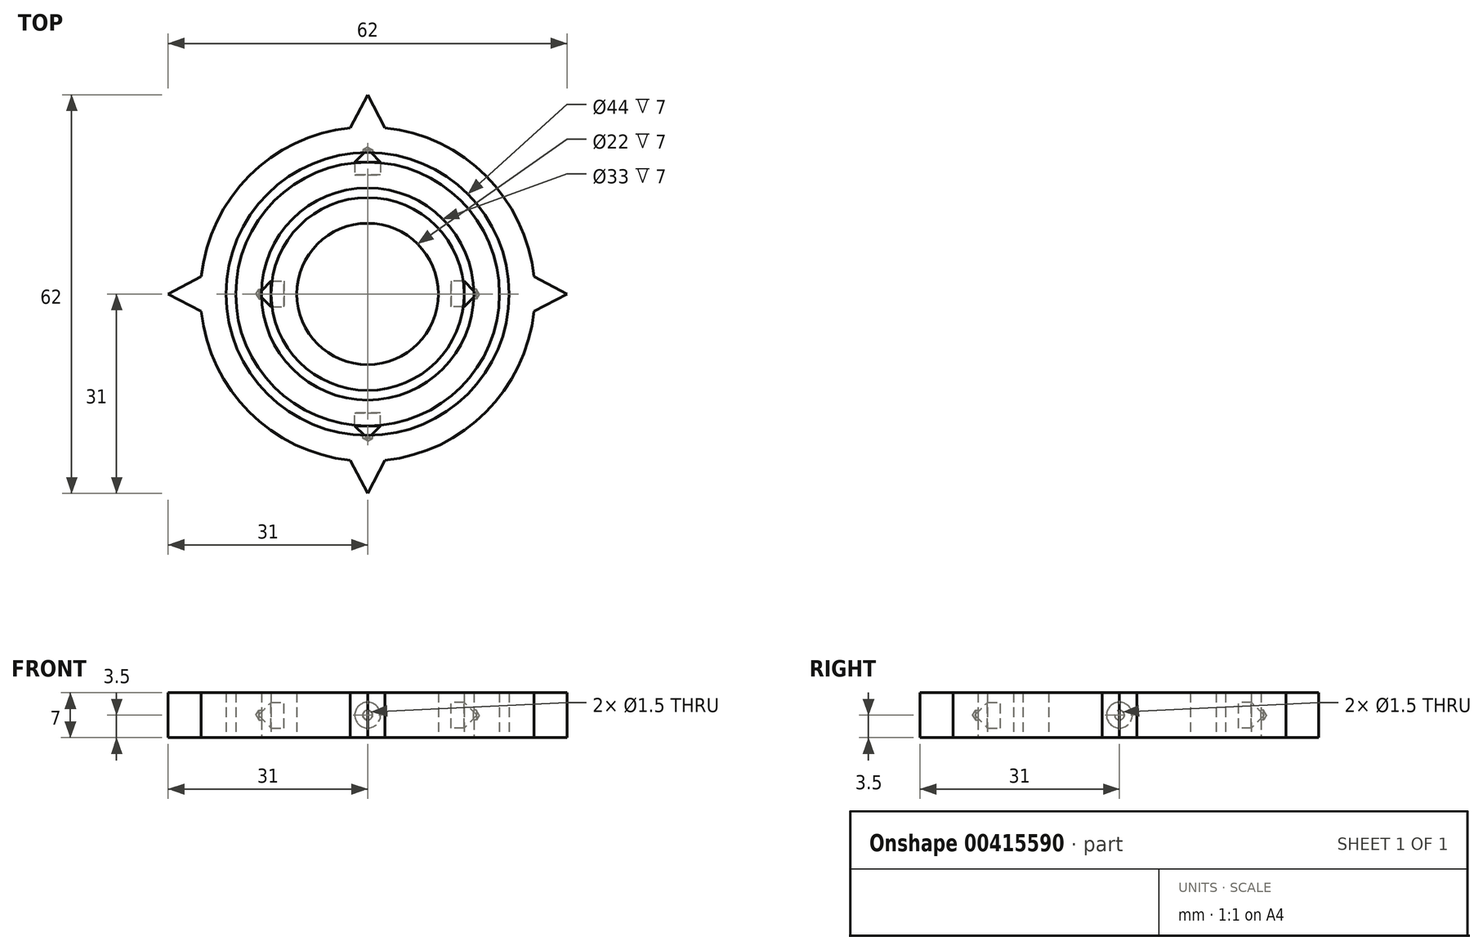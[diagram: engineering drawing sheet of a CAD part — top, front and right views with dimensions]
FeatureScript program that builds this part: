
annotation { "Feature Type Name" : "Feature", "Feature Type Description" : "" }
export const myFeature = defineFeature(function(context is Context, id is Id, definition is map)
    precondition{}
    {
        {
            var Q0;
            Q0=qCreatedBy(makeId("Top.planeOp"),FACE);
            var sketch = newSketch(context, id + "F0", { "sketchPlane" : qUnion([Q0])});
            skCircle(sketch, "E0", {"center": v(0, 0) * mm, "radius": 11 * mm});
            skCircle(sketch, "E1.0", {"center": v(0, 0) * mm, "radius": 15 * mm});
            skSolve(sketch);
        }
        {
            var Q0;
            Q0=makeQuery(id+"F0.imprint","IMPRINT",FACE,{"disambiguationData":[TD([[makeQuery(id+"F0.imprint","IMPRINT",EDGE,{"derivedFrom":sQuery(id+"F0.wireOp",EDGE,"E0")}),-1.0]])]});
            extrude(context, id + "F1", {"entities" : qUnion([Q0]), "endBound" : BoundingType.SYMMETRIC, "depth" : 7 * mm});
        }
        {
            var Q0;
            Q0=qCreatedBy(makeId("Right.planeOp"),FACE);
            cPlane(context, id + "F2", {"entities" : qUnion([Q0]), "cplaneType" : CPlaneType.OFFSET, "offset" : 13 * mm, "width" : 150 * mm, "height" : 150 * mm});
        }
        {
            var Q0;
            Q0=qCreatedBy(id+"F2.planeOp",FACE);
            var sketch = newSketch(context, id + "F3", { "sketchPlane" : qUnion([Q0])});
            skCircle(sketch, "E2", {"center": v(0, 0) * mm, "radius": 2 * mm});
            skSolve(sketch);
        }
        {
            var Q0;
            Q0=qCreatedBy(makeId("Right.planeOp"),FACE);
            cPlane(context, id + "F4", {"entities" : qUnion([Q0]), "cplaneType" : CPlaneType.OFFSET, "offset" : 16 * mm, "width" : 150 * mm, "height" : 150 * mm});
        }
        {
            var Q0;
            Q0=qCreatedBy(makeId("Right.planeOp"),FACE);
            cPlane(context, id + "F5", {"entities" : qUnion([Q0]), "cplaneType" : CPlaneType.OFFSET, "offset" : 16 * mm, "oppositeDirection" : true, "width" : 150 * mm, "height" : 150 * mm});
        }
        {
            var Q0;
            Q0=qCreatedBy(id+"F4.planeOp",FACE);
            var sketch = newSketch(context, id + "F6", { "sketchPlane" : qUnion([Q0])});
            skCircle(sketch, "E3", {"center": v(0, 0) * mm, "radius": 1.75 * mm});
            skSolve(sketch);
        }
        {
            var Q0;
            Q0=qCreatedBy(makeId("Top.planeOp"),FACE);
            var sketch = newSketch(context, id + "F7", { "sketchPlane" : qUnion([Q0])});
            skCircle(sketch, "E4", {"center": v(0, 0) * mm, "radius": 16.5 * mm});
            skCircle(sketch, "E5.0", {"center": v(0, 0) * mm, "radius": 20.5 * mm});
            skSolve(sketch);
        }
        {
            var Q0;
            Q0=qCreatedBy(id+"F5.planeOp",FACE);
            var sketch = newSketch(context, id + "F8", { "sketchPlane" : qUnion([Q0])});
            skCircle(sketch, "E6", {"center": v(0, 0) * mm, "radius": 2.58 * mm});
            skSolve(sketch);
        }
        {
            var Q0;
            Q0=makeQuery(id+"F7.imprint","IMPRINT",FACE,{"disambiguationData":[TD([[makeQuery(id+"F7.imprint","IMPRINT",EDGE,{"derivedFrom":sQuery(id+"F7.wireOp",EDGE,"E4")}),-1.0]])]});
            extrude(context, id + "F9", {"entities" : qUnion([Q0]), "endBound" : BoundingType.SYMMETRIC, "depth" : 7 * mm});
        }
        {
            var Q0;
            Q0 = qSketchRegion(id + "F3", true);
            extrude(context, id + "F10", {"entities" : qUnion([Q0]), "depth" : 4 * mm});
        }
        {
            var Q0;
            Q0=makeQuery(id+"F10.opExtrude","CAP_FACE",FACE,{"disambiguationData":[OSD([sQuery(id+"F3.wireOp",EDGE,"E2")])],"isStart":false});
            chamfer(context, id + "F11", {"entities" : qUnion([Q0]), "width" : 2 * mm, "tangentPropagation" : true});
        }
        {
            var Q0;
            Q0=sQuery(id+"F6.wireOp",VERTEX,"E3.center");
            var Q1;
            Q1=makeQuery(id+"F9.opExtrude","SWEPT_BODY",BODY,{"disambiguationData":[OSD([sQuery(id+"F7.wireOp",EDGE,"E4"),sQuery(id+"F7.wireOp",EDGE,"E5.0")])]});
            hole(context, id + "F12", {"style" : HoleStyle.SIMPLE, "endStyle" : HoleEndStyle.BLIND, "oppositeDirection" : true, "holeDiameter" : 1.5 * mm, "holeDepth" : 0.4 * mm, "isTappedThrough" : true, "tappedDepth" : 12 * mm, "tapClearance" : 3, "locations" : qUnion([Q0]), "scope" : qUnion([Q1])});
        }
        {
            var Q0;
            Q0=sQuery(id+"F8.wireOp",VERTEX,"E6.center");
            var Q1;
            Q1=makeQuery(id+"F9.opExtrude","SWEPT_BODY",BODY,{"disambiguationData":[OSD([sQuery(id+"F7.wireOp",EDGE,"E4"),sQuery(id+"F7.wireOp",EDGE,"E5.0")])]});
            hole(context, id + "F13", {"style" : HoleStyle.SIMPLE, "endStyle" : HoleEndStyle.BLIND, "holeDiameter" : 1.5 * mm, "holeDepth" : 0.4 * mm, "isTappedThrough" : true, "tappedDepth" : 12 * mm, "tapClearance" : 3, "locations" : qUnion([Q0]), "scope" : qUnion([Q1])});
        }
        {
            var Q0;
            Q0=makeQuery(id+"F10.opExtrude","SWEPT_BODY",BODY,{"disambiguationData":[OSD([sQuery(id+"F3.wireOp",EDGE,"E2")])]});
            var Q1;
            Q1=qCreatedBy(makeId("Right.planeOp"),FACE);
            mirror(context, id + "F14", {"entities" : qUnion([Q0]), "mirrorPlane" : qUnion([Q1])});
        }
        {
            var Q0;
            Q0=qCreatedBy(makeId("Top.planeOp"),FACE);
            var sketch = newSketch(context, id + "F15", { "sketchPlane" : qUnion([Q0])});
            skCircle(sketch, "E7.0", {"center": v(0, 0) * mm, "radius": 22 * mm});
            skCircle(sketch, "E8.0", {"center": v(0, 0) * mm, "radius": 26 * mm});
            skPoint(sketch, "E9", {"position": v(0, 26) * mm});
            skPoint(sketch, "E10", {"position": v(26, 0) * mm});
            skPoint(sketch, "E11", {"position": v(0, -26) * mm});
            skPoint(sketch, "E12", {"position": v(-26, 0) * mm});
            skLineSegment(sketch, "E13", {"start": v(0, 31) * mm, "end": v(-2.7, 25.86) * mm});
            skLineSegment(sketch, "E14.MirrorCS", {"start": v(0, 31) * mm, "end": v(2.7, 25.86) * mm});
            skLineSegment(sketch, "E15.1.0", {"start": v(31, 0) * mm, "end": v(25.86, 2.7) * mm});
            skLineSegment(sketch, "E15.1.1", {"start": v(31, 0) * mm, "end": v(25.86, -2.7) * mm});
            skLineSegment(sketch, "E15.2.0", {"start": v(0, -31) * mm, "end": v(2.7, -25.86) * mm});
            skLineSegment(sketch, "E15.2.1", {"start": v(0, -31) * mm, "end": v(-2.7, -25.86) * mm});
            skLineSegment(sketch, "E15.3.0", {"start": v(-31, 0) * mm, "end": v(-25.86, -2.7) * mm});
            skLineSegment(sketch, "E15.3.1", {"start": v(-31, 0) * mm, "end": v(-25.86, 2.7) * mm});
            skLineSegment(sketch, "E15.anchor1", {"start": v(0, 0) * mm, "end": v(-2.7, 25.86) * mm, "construction": true});
            skLineSegment(sketch, "E15.anchor2", {"start": v(0, 0) * mm, "end": v(-25.86, -2.7) * mm, "construction": true});
            skSolve(sketch);
        }
        {
            var Q0;
            Q0=makeQuery(id+"F15.imprint","IMPRINT",FACE,{"disambiguationData":[TD([[makeQuery(id+"F15.imprint","IMPRINT",EDGE,{"derivedFrom":sQuery(id+"F15.wireOp",EDGE,"E7.0")}),-1.0]])]});
            extrude(context, id + "F16", {"entities" : qUnion([Q0]), "endBound" : BoundingType.SYMMETRIC, "depth" : 7 * mm});
        }
        {
            var Q0;
            Q0=qCreatedBy(makeId("Front.planeOp"),FACE);
            cPlane(context, id + "F17", {"entities" : qUnion([Q0]), "cplaneType" : CPlaneType.OFFSET, "offset" : 18.5 * mm, "width" : 150 * mm, "height" : 150 * mm});
        }
        {
            var Q0;
            Q0=qCreatedBy(id+"F17.planeOp",FACE);
            var sketch = newSketch(context, id + "F18", { "sketchPlane" : qUnion([Q0])});
            skCircle(sketch, "E16", {"center": v(0, 0) * mm, "radius": 2 * mm});
            skSolve(sketch);
        }
        {
            var Q0;
            Q0 = qSketchRegion(id + "F18", true);
            extrude(context, id + "F19", {"entities" : qUnion([Q0]), "depth" : 4 * mm});
        }
        {
            var Q0;
            Q0=makeQuery(id+"F19.opExtrude","CAP_FACE",FACE,{"disambiguationData":[OSD([sQuery(id+"F18.wireOp",EDGE,"E16")])],"isStart":false});
            chamfer(context, id + "F20", {"entities" : qUnion([Q0]), "width" : 2 * mm, "tangentPropagation" : true});
        }
        {
            var Q0;
            Q0=qCreatedBy(makeId("Front.planeOp"),FACE);
            cPlane(context, id + "F21", {"entities" : qUnion([Q0]), "cplaneType" : CPlaneType.OFFSET, "offset" : 21.6 * mm, "width" : 150 * mm, "height" : 150 * mm});
        }
        {
            var Q0;
            Q0=qCreatedBy(id+"F21.planeOp",FACE);
            var sketch = newSketch(context, id + "F22", { "sketchPlane" : qUnion([Q0])});
            skCircle(sketch, "E17", {"center": v(0, 0) * mm, "radius": 2.03 * mm});
            skSolve(sketch);
        }
        {
            var Q0;
            Q0=sQuery(id+"F22.wireOp",VERTEX,"E17.center");
            var Q1;
            Q1=makeQuery(id+"F16.opExtrude","SWEPT_BODY",BODY,{"disambiguationData":[OSD([sQuery(id+"F15.wireOp",EDGE,"E7.0"),sQuery(id+"F15.wireOp",EDGE,"E8.0")])]});
            hole(context, id + "F23", {"style" : HoleStyle.SIMPLE, "endStyle" : HoleEndStyle.BLIND, "oppositeDirection" : true, "holeDiameter" : 1.5 * mm, "holeDepth" : 0.4 * mm, "isTappedThrough" : true, "tappedDepth" : 12 * mm, "tapClearance" : 3, "locations" : qUnion([Q0]), "scope" : qUnion([Q1])});
        }
        {
            var Q0;
            Q0=qCreatedBy(makeId("Front.planeOp"),FACE);
            cPlane(context, id + "F24", {"entities" : qUnion([Q0]), "cplaneType" : CPlaneType.OFFSET, "offset" : 21.5 * mm, "oppositeDirection" : true, "width" : 150 * mm, "height" : 150 * mm});
        }
        {
            var Q0;
            Q0=qCreatedBy(id+"F24.planeOp",FACE);
            var sketch = newSketch(context, id + "F25", { "sketchPlane" : qUnion([Q0])});
            skCircle(sketch, "E18", {"center": v(0, 0) * mm, "radius": 2 * mm});
            skSolve(sketch);
        }
        {
            var Q0;
            Q0=sQuery(id+"F25.wireOp",VERTEX,"E18.center");
            var Q1;
            Q1=makeQuery(id+"F16.opExtrude","SWEPT_BODY",BODY,{"disambiguationData":[OSD([sQuery(id+"F15.wireOp",EDGE,"E7.0"),sQuery(id+"F15.wireOp",EDGE,"E8.0")])]});
            hole(context, id + "F26", {"style" : HoleStyle.SIMPLE, "endStyle" : HoleEndStyle.BLIND, "holeDiameter" : 1.5 * mm, "holeDepth" : 0.4 * mm, "isTappedThrough" : true, "tappedDepth" : 12 * mm, "tapClearance" : 3, "locations" : qUnion([Q0]), "scope" : qUnion([Q1])});
        }
        {
            var Q0;
            Q0=makeQuery(id+"F19.opExtrude","SWEPT_BODY",BODY,{"disambiguationData":[OSD([sQuery(id+"F18.wireOp",EDGE,"E16")])]});
            var Q1;
            Q1=qCreatedBy(makeId("Front.planeOp"),FACE);
            mirror(context, id + "F27", {"entities" : qUnion([Q0]), "mirrorPlane" : qUnion([Q1])});
        }
        {
            var Q0;
            {var subQ0=sQuery(id+"F15.wireOp",EDGE,"E13");Q0=makeQuery(id+"F15.imprint","IMPRINT",FACE,{"disambiguationData":[TD([[makeQuery(id+"F15.imprint","IMPRINT",EDGE,{"derivedFrom":subQ0}),1.0]])]});}
            var Q1;
            {var subQ0=sQuery(id+"F15.wireOp",EDGE,"E15.1.0");Q1=makeQuery(id+"F15.imprint","IMPRINT",FACE,{"disambiguationData":[TD([[makeQuery(id+"F15.imprint","IMPRINT",EDGE,{"derivedFrom":subQ0}),1.0]])]});}
            var Q2;
            {var subQ0=sQuery(id+"F15.wireOp",EDGE,"E15.3.0");Q2=makeQuery(id+"F15.imprint","IMPRINT",FACE,{"disambiguationData":[TD([[makeQuery(id+"F15.imprint","IMPRINT",EDGE,{"derivedFrom":subQ0}),1.0]])]});}
            var Q3;
            {var subQ0=sQuery(id+"F15.wireOp",EDGE,"E15.2.0");Q3=makeQuery(id+"F15.imprint","IMPRINT",FACE,{"disambiguationData":[TD([[makeQuery(id+"F15.imprint","IMPRINT",EDGE,{"derivedFrom":subQ0}),1.0]])]});}
            extrude(context, id + "F28", {"entities" : qUnion([Q0, Q1, Q2, Q3]), "operationType" : NewBodyOperationType.ADD, "endBound" : BoundingType.SYMMETRIC, "depth" : 7 * mm});
        }
    });
